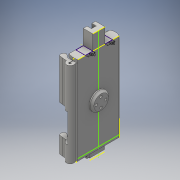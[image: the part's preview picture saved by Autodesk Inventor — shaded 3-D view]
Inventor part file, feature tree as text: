
AUTODESK INVENTOR PART (.ipt)
format: ipt  version: 2016 (Build 200138000, 138)  size: 699,392 bytes
history: native  units: in
note: dims shown in document units (in); Inventor stores cm internally (conversion verified against a paired STEP export)
features: sketch x12, extrude x6, plane x2, split x2, chamfer x1, hole x1
ambient origin geometry x8: Origin, YZ Plane, XZ Plane, XY Plane, X Axis, Y Axis, Z Axis, Center Point
bodies: Solid1 (feature_tree)
feature tree (24):
  extrude  "Extrusion1"  Depth=0.2in
  sketch  "Sketch2"  dims[d9=0.2in d10=0.2in]
  plane  "Work Plane1"
  split  "Split2"
  extrude  "Extrusion2"  Depth=0.2in
  split  "Split3"
  extrude  "Extrusion3"  Depth=0.2in
  extrude  "Extrusion4"  Depth=0.2in
  sketch  "Sketch8"  dims[d26=20.0in]
  plane  "Work Plane2"
  extrude  "Extrusion5"  TaperAngle=60.0deg  [1 undecoded]
  extrude  "Extrusion6"  Depth=5.7in
  chamfer  "Chamfer1"  Distance=0.2in
  hole  "Hole1"  [1 undecoded]
  sketch  "Sketch13"  dims[d32=90.0deg d33=0.2in d34=0.0in d35=0.3in d36=2.904in d37=0.42in d39=0.31in d40=0.2in d41=0.2in d42=0.33in d43=0.0in d44=0.33in d45=0.0in d46=0.5in d47=0.5in d48=1.0in d49=1.0in d50=0.0in d51=1.222in d52=0.1969in d53=0.0in d54=0.125in d55=0.125in d56=45.0deg d66=0.2362in d67=0.7874in d69=0.445in d70=0.7874in d72=0.445in d75=0.1575in d76=0.75in d77=0.2362in d78=0.1181in d79=0.5635in d80=1.0in d81=0.8108in]
  sketch  "Sketch1"  dims[d6=0.2in d8=0.2in]
  sketch  "Sketch3"  dims[d12=0.2in d13=0.2in]
  sketch  "Sketch4"  dims[d15=0.2in d17=0.2in]
  sketch  "Sketch5"  dims[d20=0.2in d21=60.0deg]
  sketch  "Sketch6"  dims[d22=5.7in d23=0.0in d24=0.14in]
  sketch  "Sketch7"  dims[d25=0.14in]
  sketch  "Sketch9"  dims[d27=0.28in]
  sketch  "Sketch10"  dims[d28=0.28in]
  sketch  "Sketch12"  dims[d29=0.14in]
note: 2 required parameter values undecoded (feature->parameter linkage not recoverable at this tier; creation-order binding heuristic only, values carry confidence <= 0.55)
